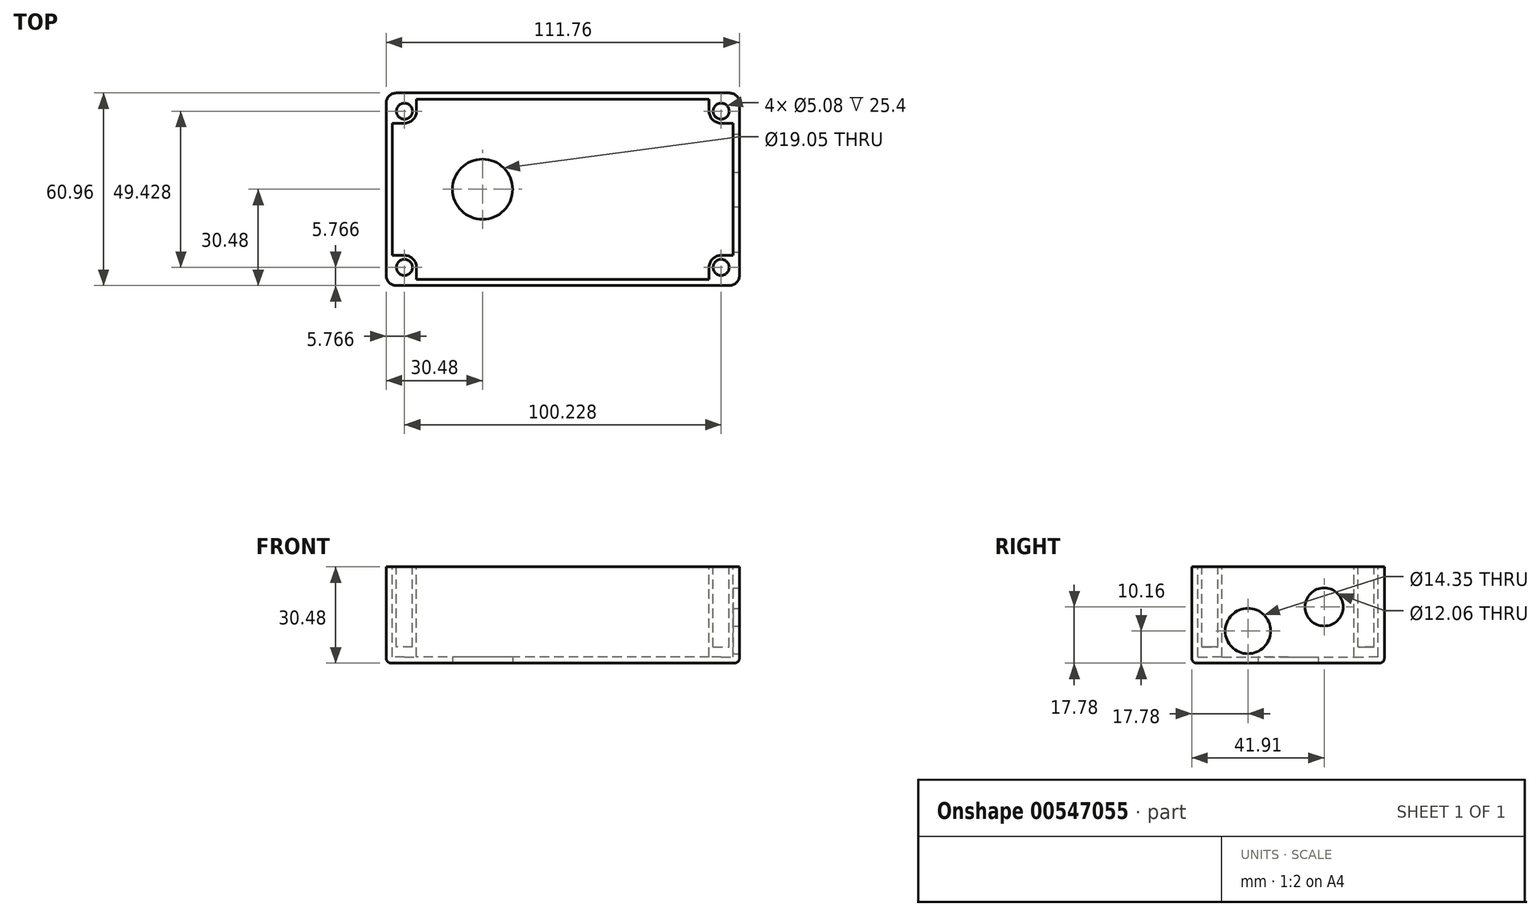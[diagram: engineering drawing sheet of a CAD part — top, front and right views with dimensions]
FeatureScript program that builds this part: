
annotation { "Feature Type Name" : "Feature", "Feature Type Description" : "" }
export const myFeature = defineFeature(function(context is Context, id is Id, definition is map)
    precondition{}
    {
        {
            var Q0;
            Q0=qCreatedBy(makeId("Top.planeOp"),FACE);
            var sketch = newSketch(context, id + "F0", { "sketchPlane" : qUnion([Q0])});
            skLineSegment(sketch, "E0.bottom", {"start": v(55.88, -30.48) * mm, "end": v(-55.88, -30.48) * mm});
            skLineSegment(sketch, "E0.top", {"start": v(55.88, 30.48) * mm, "end": v(-55.88, 30.48) * mm});
            skLineSegment(sketch, "E0.left", {"start": v(55.88, -30.48) * mm, "end": v(55.88, 30.48) * mm});
            skLineSegment(sketch, "E0.right", {"start": v(-55.88, -30.48) * mm, "end": v(-55.88, 30.48) * mm});
            skPoint(sketch, "E0.middle", {"position": v(0, 0) * mm});
            skSolve(sketch);
        }
        {
            var Q0;
            Q0=makeQuery(id+"F0.imprint","IMPRINT",FACE,{"disambiguationData":[TD([[makeQuery(id+"F0.imprint","IMPRINT",EDGE,{"derivedFrom":sQuery(id+"F0.wireOp",EDGE,"E0.bottom")}),-1.0]])]});
            extrude(context, id + "F1", {"entities" : qUnion([Q0]), "depth" : 30.48 * mm, "offsetDistance" : 25.4 * mm});
        }
        {
            var Q0;
            Q0=makeQuery(id+"F1.opExtrude","CAP_FACE",FACE,{"disambiguationData":[OSD([sQuery(id+"F0.wireOp",EDGE,"E0.bottom"),sQuery(id+"F0.wireOp",EDGE,"E0.top"),sQuery(id+"F0.wireOp",EDGE,"E0.left"),sQuery(id+"F0.wireOp",EDGE,"E0.right")])],"isStart":false});
            var Q1;
            Q1=makeQuery(id+"F1.opExtrude","SWEPT_BODY",BODY,{"disambiguationData":[OSD([sQuery(id+"F0.wireOp",EDGE,"E0.bottom"),sQuery(id+"F0.wireOp",EDGE,"E0.top"),sQuery(id+"F0.wireOp",EDGE,"E0.left"),sQuery(id+"F0.wireOp",EDGE,"E0.right")])]});
            shell(context, id + "F2", {"entities" : qUnion([Q0]), "parts" : qUnion([Q1]), "thickness" : 1.96 * mm});
        }
        {
            var Q0;
            Q0=makeQuery(id+"F1.opExtrude","CAP_FACE",FACE,{"disambiguationData":[OSD([sQuery(id+"F0.wireOp",EDGE,"E0.bottom"),sQuery(id+"F0.wireOp",EDGE,"E0.top"),sQuery(id+"F0.wireOp",EDGE,"E0.left"),sQuery(id+"F0.wireOp",EDGE,"E0.right")])],"isStart":false});
            var sketch = newSketch(context, id + "F3", { "sketchPlane" : qUnion([Q0])});
            skArc(sketch, "E1", {"start": v(-50.11, 20.9) * mm, "mid": v(-47.42, 22.02) * mm, "end": v(-46.3, 24.71) * mm});
            skLineSegment(sketch, "E2", {"start": v(-46.3, 24.71) * mm, "end": v(-46.3, 28.52) * mm});
            skLineSegment(sketch, "E3", {"start": v(-46.3, 28.52) * mm, "end": v(-53.92, 28.52) * mm});
            skLineSegment(sketch, "E4", {"start": v(-53.92, 28.52) * mm, "end": v(-53.92, 20.9) * mm});
            skLineSegment(sketch, "E5", {"start": v(-53.92, 20.9) * mm, "end": v(-50.11, 20.9) * mm});
            skSolve(sketch);
        }
        {
            var Q0;
            Q0 = qSketchRegion(id + "F3", true);
            extrude(context, id + "F4", {"entities" : qUnion([Q0]), "endBound" : BoundingType.UP_TO_NEXT, "oppositeDirection" : true, "depth" : 25.4 * mm, "offsetDistance" : 25.4 * mm});
        }
        {
            var Q0;
            Q0=makeQuery(id+"F4.opExtrude","CAP_FACE",FACE,{"disambiguationData":[OSD([sQuery(id+"F3.wireOp",EDGE,"E1"),sQuery(id+"F3.wireOp",EDGE,"E2"),sQuery(id+"F3.wireOp",EDGE,"E3"),sQuery(id+"F3.wireOp",EDGE,"E4"),sQuery(id+"F3.wireOp",EDGE,"E5")])],"isStart":true});
            var sketch = newSketch(context, id + "F5", { "sketchPlane" : qUnion([Q0])});
            skCircle(sketch, "E6", {"center": v(-50.11, 24.71) * mm, "radius": 2.54 * mm});
            skSolve(sketch);
        }
        {
            var Q0;
            Q0 = qSketchRegion(id + "F5", true);
            extrude(context, id + "F6", {"entities" : qUnion([Q0]), "operationType" : NewBodyOperationType.REMOVE, "oppositeDirection" : true, "depth" : 25.4 * mm, "offsetDistance" : 25.4 * mm});
        }
        {
            var Q0;
            Q0=makeQuery(id+"F4.opExtrude","SWEPT_BODY",BODY,{"disambiguationData":[OSD([sQuery(id+"F3.wireOp",EDGE,"E1"),sQuery(id+"F3.wireOp",EDGE,"E2"),sQuery(id+"F3.wireOp",EDGE,"E3"),sQuery(id+"F3.wireOp",EDGE,"E4"),sQuery(id+"F3.wireOp",EDGE,"E5")])]});
            var Q1;
            Q1=qCreatedBy(makeId("Right.planeOp"),FACE);
            mirror(context, id + "F7", {"entities" : qUnion([Q0]), "mirrorPlane" : qUnion([Q1])});
        }
        {
            var Q0;
            Q0=makeQuery(id+"F4.opExtrude","SWEPT_BODY",BODY,{"disambiguationData":[OSD([sQuery(id+"F3.wireOp",EDGE,"E1"),sQuery(id+"F3.wireOp",EDGE,"E2"),sQuery(id+"F3.wireOp",EDGE,"E3"),sQuery(id+"F3.wireOp",EDGE,"E4"),sQuery(id+"F3.wireOp",EDGE,"E5")])]});
            var Q1;
            Q1=makeQuery(id+"F7.opPattern","COPY",BODY,{"derivedFrom":makeQuery(id+"F4.opExtrude","SWEPT_BODY",BODY,{"disambiguationData":[OSD([sQuery(id+"F3.wireOp",EDGE,"E1"),sQuery(id+"F3.wireOp",EDGE,"E2"),sQuery(id+"F3.wireOp",EDGE,"E3"),sQuery(id+"F3.wireOp",EDGE,"E4"),sQuery(id+"F3.wireOp",EDGE,"E5")])]}),"instanceName":"1"});
            var Q2;
            Q2=qCreatedBy(makeId("Front.planeOp"),FACE);
            mirror(context, id + "F8", {"operationType" : NewBodyOperationType.ADD, "entities" : qUnion([Q0, Q1]), "mirrorPlane" : qUnion([Q2])});
        }
        {
            var Q0;
            Q0=makeQuery(id+"F1.opExtrude","SWEPT_EDGE",EDGE,{"disambiguationData":[OSD([sQuery(id+"F0.wireOp",EDGE,"E0.top"),sQuery(id+"F0.wireOp",EDGE,"E0.right")])]});
            var Q1;
            Q1=makeQuery(id+"F1.opExtrude","SWEPT_EDGE",EDGE,{"disambiguationData":[OSD([sQuery(id+"F0.wireOp",EDGE,"E0.bottom"),sQuery(id+"F0.wireOp",EDGE,"E0.right")])]});
            var Q2;
            Q2=makeQuery(id+"F1.opExtrude","SWEPT_EDGE",EDGE,{"disambiguationData":[OSD([sQuery(id+"F0.wireOp",EDGE,"E0.bottom"),sQuery(id+"F0.wireOp",EDGE,"E0.left")])]});
            var Q3;
            Q3=makeQuery(id+"F1.opExtrude","SWEPT_EDGE",EDGE,{"disambiguationData":[OSD([sQuery(id+"F0.wireOp",EDGE,"E0.top"),sQuery(id+"F0.wireOp",EDGE,"E0.left")])]});
            fillet(context, id + "F9", {"entities" : qUnion([Q0, Q1, Q2, Q3]), "radius" : 3.17 * mm, "tangentPropagation" : true, "allowEdgeOverflow" : false});
        }
        {
            var Q0;
            Q0=makeQuery(id+"F1.opExtrude","CAP_FACE",FACE,{"disambiguationData":[OSD([sQuery(id+"F0.wireOp",EDGE,"E0.bottom"),sQuery(id+"F0.wireOp",EDGE,"E0.top"),sQuery(id+"F0.wireOp",EDGE,"E0.left"),sQuery(id+"F0.wireOp",EDGE,"E0.right")])],"isStart":true});
            fillet(context, id + "F10", {"entities" : qUnion([Q0]), "radius" : 1.59 * mm, "tangentPropagation" : true, "allowEdgeOverflow" : false});
        }
        {
            var Q0;
            Q0=makeQuery(id+"F1.opExtrude","SWEPT_FACE",FACE,{"disambiguationData":[OSD([sQuery(id+"F0.wireOp",EDGE,"E0.left")])]});
            var sketch = newSketch(context, id + "F11", { "sketchPlane" : qUnion([Q0])});
            skCircle(sketch, "E7", {"center": v(-12.7, 10.16) * mm, "radius": 7.18 * mm});
            skSolve(sketch);
        }
        {
            var Q0;
            Q0 = qSketchRegion(id + "F11", true);
            extrude(context, id + "F12", {"entities" : qUnion([Q0]), "operationType" : NewBodyOperationType.REMOVE, "endBound" : BoundingType.UP_TO_NEXT, "oppositeDirection" : true, "depth" : 25.4 * mm, "offsetDistance" : 25.4 * mm});
        }
        {
            var Q0;
            Q0=makeQuery(id+"F1.opExtrude","SWEPT_FACE",FACE,{"disambiguationData":[OSD([sQuery(id+"F0.wireOp",EDGE,"E0.left")])]});
            var sketch = newSketch(context, id + "F13", { "sketchPlane" : qUnion([Q0])});
            skCircle(sketch, "E8", {"center": v(11.43, 17.78) * mm, "radius": 6.03 * mm});
            skSolve(sketch);
        }
        {
            var Q0;
            Q0 = qSketchRegion(id + "F13", true);
            extrude(context, id + "F14", {"entities" : qUnion([Q0]), "operationType" : NewBodyOperationType.REMOVE, "endBound" : BoundingType.UP_TO_NEXT, "oppositeDirection" : true, "depth" : 25.4 * mm, "offsetDistance" : 25.4 * mm});
        }
        {
            var Q0;
            Q0=makeQuery(id+"F1.opExtrude","CAP_FACE",FACE,{"disambiguationData":[OSD([sQuery(id+"F0.wireOp",EDGE,"E0.bottom"),sQuery(id+"F0.wireOp",EDGE,"E0.top"),sQuery(id+"F0.wireOp",EDGE,"E0.left"),sQuery(id+"F0.wireOp",EDGE,"E0.right")])],"isStart":true});
            var sketch = newSketch(context, id + "F15", { "sketchPlane" : qUnion([Q0])});
            skCircle(sketch, "E9", {"center": v(-25.4, 0) * mm, "radius": 9.53 * mm});
            skSolve(sketch);
        }
        {
            var Q0;
            Q0 = qSketchRegion(id + "F15", true);
            extrude(context, id + "F16", {"entities" : qUnion([Q0]), "operationType" : NewBodyOperationType.REMOVE, "endBound" : BoundingType.THROUGH_ALL, "oppositeDirection" : true, "depth" : 25.4 * mm, "offsetDistance" : 25.4 * mm});
        }
    });
